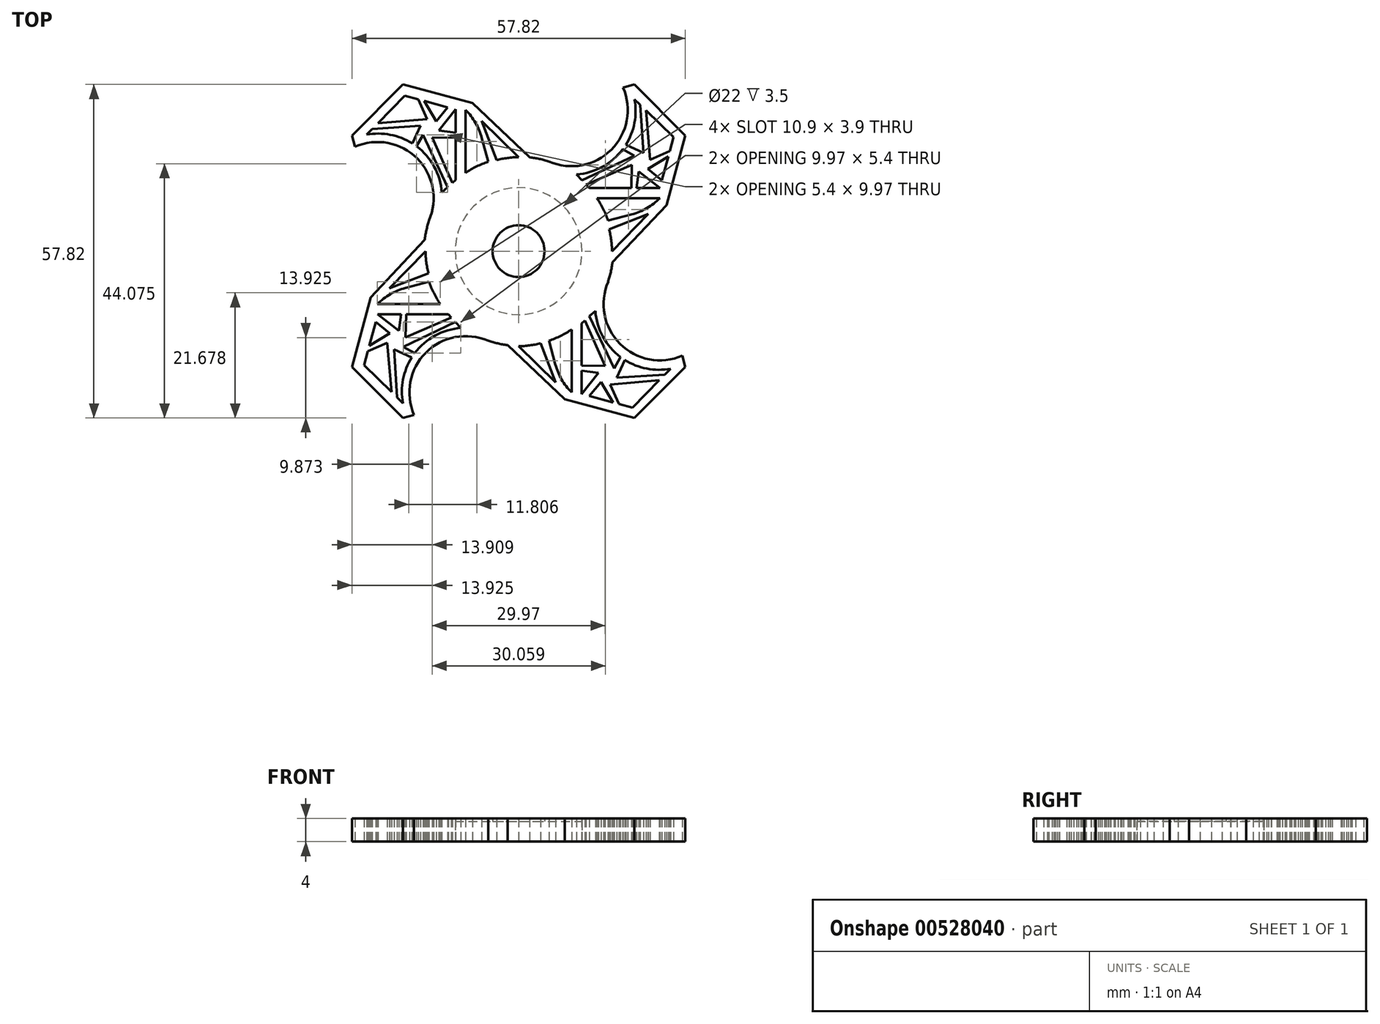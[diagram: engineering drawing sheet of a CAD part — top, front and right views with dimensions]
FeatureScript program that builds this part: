
annotation { "Feature Type Name" : "Feature", "Feature Type Description" : "" }
export const myFeature = defineFeature(function(context is Context, id is Id, definition is map)
    precondition{}
    {
        {
            var Q0;
            Q0=qCreatedBy(makeId("Top.planeOp"),FACE);
            var sketch = newSketch(context, id + "F0", { "sketchPlane" : qUnion([Q0])});
            skCircle(sketch, "E0", {"center": v(0, 0) * mm, "radius": 16.4 * mm});
            skSolve(sketch);
        }
        {
            var Q0;
            Q0 = qSketchRegion(id + "F0", true);
            extrude(context, id + "F1", {"entities" : qUnion([Q0]), "depth" : 4 * mm, "offsetDistance" : 25 * mm});
        }
        {
            var Q0;
            Q0=qCreatedBy(makeId("Top.planeOp"),FACE);
            var sketch = newSketch(context, id + "F2", { "sketchPlane" : qUnion([Q0])});
            skPoint(sketch, "E1", {"position": v(0, 0) * mm});
            skSolve(sketch);
        }
        {
            var Q0;
            Q0=qCreatedBy(makeId("Top.planeOp"),FACE);
            var sketch = newSketch(context, id + "F3", { "sketchPlane" : qUnion([Q0])});
            skLineSegment(sketch, "E2.bottom", {"start": v(-9.18, 9.18) * mm, "end": v(-24.49, 9.18) * mm});
            skLineSegment(sketch, "E2.top", {"start": v(-9.18, 24.49) * mm, "end": v(-24.49, 24.49) * mm});
            skLineSegment(sketch, "E2.left", {"start": v(-9.18, 9.18) * mm, "end": v(-9.18, 24.49) * mm});
            skLineSegment(sketch, "E2.right", {"start": v(-24.49, 9.18) * mm, "end": v(-24.49, 24.49) * mm});
            skPoint(sketch, "E3.oppositeSnap0", {"position": v(-16.84, 9.18) * mm});
            skLineSegment(sketch, "E4.bottom", {"start": v(-9.18, -9.18) * mm, "end": v(-24.49, -9.18) * mm});
            skLineSegment(sketch, "E4.top", {"start": v(-9.18, -24.49) * mm, "end": v(-24.49, -24.49) * mm});
            skLineSegment(sketch, "E4.left", {"start": v(-9.18, -9.18) * mm, "end": v(-9.18, -24.49) * mm});
            skLineSegment(sketch, "E4.right", {"start": v(-24.49, -9.18) * mm, "end": v(-24.49, -24.49) * mm});
            skLineSegment(sketch, "E5.bottom", {"start": v(9.18, -9.18) * mm, "end": v(24.49, -9.18) * mm});
            skLineSegment(sketch, "E5.top", {"start": v(9.18, -24.49) * mm, "end": v(24.49, -24.49) * mm});
            skLineSegment(sketch, "E5.left", {"start": v(9.18, -9.18) * mm, "end": v(9.18, -24.49) * mm});
            skLineSegment(sketch, "E5.right", {"start": v(24.49, -9.18) * mm, "end": v(24.49, -24.49) * mm});
            skLineSegment(sketch, "E6.bottom", {"start": v(9.18, 9.18) * mm, "end": v(24.49, 9.18) * mm});
            skLineSegment(sketch, "E6.top", {"start": v(9.18, 24.49) * mm, "end": v(24.49, 24.49) * mm});
            skLineSegment(sketch, "E6.left", {"start": v(9.18, 9.18) * mm, "end": v(9.18, 24.49) * mm});
            skLineSegment(sketch, "E6.right", {"start": v(24.49, 9.18) * mm, "end": v(24.49, 24.49) * mm});
            skCircle(sketch, "E7", {"center": v(16.84, -16.84) * mm, "radius": 10.82 * mm});
            skCircle(sketch, "E8", {"center": v(16.84, 16.84) * mm, "radius": 10.82 * mm});
            skCircle(sketch, "E9", {"center": v(-16.84, 16.84) * mm, "radius": 10.82 * mm});
            skCircle(sketch, "E10", {"center": v(-16.84, -16.84) * mm, "radius": 10.82 * mm});
            skCircle(sketch, "E11.cCircle", {"center": v(16.84, -16.84) * mm, "radius": 10.82 * mm, "construction": true});
            skLineSegment(sketch, "E11.0", {"start": v(28.9, -20.07) * mm, "end": v(20.07, -28.9) * mm});
            skLineSegment(sketch, "E11.1", {"start": v(20.07, -28.9) * mm, "end": v(8, -25.67) * mm});
            skLineSegment(sketch, "E11.2", {"start": v(8, -25.67) * mm, "end": v(4.76, -13.6) * mm});
            skLineSegment(sketch, "E11.3", {"start": v(4.76, -13.6) * mm, "end": v(13.6, -4.76) * mm});
            skLineSegment(sketch, "E11.4", {"start": v(13.6, -4.76) * mm, "end": v(25.67, -8) * mm});
            skLineSegment(sketch, "E11.5", {"start": v(25.67, -8) * mm, "end": v(28.9, -20.07) * mm});
            skPoint(sketch, "E11.0.midPoint", {"position": v(24.49, -24.49) * mm});
            skCircle(sketch, "E12.cCircle", {"center": v(-16.84, -16.84) * mm, "radius": 10.82 * mm, "construction": true});
            skLineSegment(sketch, "E12.0", {"start": v(-20.07, -28.9) * mm, "end": v(-28.9, -20.07) * mm});
            skLineSegment(sketch, "E12.1", {"start": v(-28.9, -20.07) * mm, "end": v(-25.67, -8) * mm});
            skLineSegment(sketch, "E12.2", {"start": v(-25.67, -8) * mm, "end": v(-13.6, -4.76) * mm});
            skLineSegment(sketch, "E12.3", {"start": v(-13.6, -4.76) * mm, "end": v(-4.76, -13.6) * mm});
            skLineSegment(sketch, "E12.4", {"start": v(-4.76, -13.6) * mm, "end": v(-8, -25.67) * mm});
            skLineSegment(sketch, "E12.5", {"start": v(-8, -25.67) * mm, "end": v(-20.07, -28.9) * mm});
            skPoint(sketch, "E12.0.midPoint", {"position": v(-24.49, -24.49) * mm});
            skCircle(sketch, "E13.cCircle", {"center": v(16.84, 16.84) * mm, "radius": 10.82 * mm, "construction": true});
            skLineSegment(sketch, "E13.0", {"start": v(20.07, 28.9) * mm, "end": v(28.9, 20.07) * mm});
            skLineSegment(sketch, "E13.1", {"start": v(28.9, 20.07) * mm, "end": v(25.67, 8) * mm});
            skLineSegment(sketch, "E13.2", {"start": v(25.67, 8) * mm, "end": v(13.6, 4.76) * mm});
            skLineSegment(sketch, "E13.3", {"start": v(13.6, 4.76) * mm, "end": v(4.76, 13.6) * mm});
            skLineSegment(sketch, "E13.4", {"start": v(4.76, 13.6) * mm, "end": v(8, 25.67) * mm});
            skLineSegment(sketch, "E13.5", {"start": v(8, 25.67) * mm, "end": v(20.07, 28.9) * mm});
            skPoint(sketch, "E13.0.midPoint", {"position": v(24.49, 24.49) * mm});
            skCircle(sketch, "E14.cCircle", {"center": v(-16.84, 16.84) * mm, "radius": 10.82 * mm, "construction": true});
            skLineSegment(sketch, "E14.0", {"start": v(-28.9, 20.07) * mm, "end": v(-20.07, 28.9) * mm});
            skLineSegment(sketch, "E14.1", {"start": v(-20.07, 28.9) * mm, "end": v(-8, 25.67) * mm});
            skLineSegment(sketch, "E14.2", {"start": v(-8, 25.67) * mm, "end": v(-4.76, 13.6) * mm});
            skLineSegment(sketch, "E14.3", {"start": v(-4.76, 13.6) * mm, "end": v(-13.6, 4.76) * mm});
            skLineSegment(sketch, "E14.4", {"start": v(-13.6, 4.76) * mm, "end": v(-25.67, 8) * mm});
            skLineSegment(sketch, "E14.5", {"start": v(-25.67, 8) * mm, "end": v(-28.9, 20.07) * mm});
            skPoint(sketch, "E14.0.midPoint", {"position": v(-24.49, 24.49) * mm});
            skLineSegment(sketch, "E15", {"start": v(-8, 25.67) * mm, "end": v(4.76, 13.6) * mm});
            skLineSegment(sketch, "E16", {"start": v(4.76, 13.6) * mm, "end": v(-4.76, 13.6) * mm});
            skLineSegment(sketch, "E17", {"start": v(25.67, 8) * mm, "end": v(13.6, -4.76) * mm});
            skLineSegment(sketch, "E18", {"start": v(13.6, 4.76) * mm, "end": v(13.6, -4.76) * mm});
            skLineSegment(sketch, "E19", {"start": v(-25.67, -8) * mm, "end": v(-13.6, 4.76) * mm});
            skLineSegment(sketch, "E20", {"start": v(-13.6, 4.76) * mm, "end": v(-13.6, -4.76) * mm});
            skLineSegment(sketch, "E21", {"start": v(8, -25.67) * mm, "end": v(-4.76, -13.6) * mm});
            skLineSegment(sketch, "E22", {"start": v(-4.76, -13.6) * mm, "end": v(4.76, -13.6) * mm});
            skSolve(sketch);
        }
        {
            var Q0;
            Q0 = qSketchRegion(id + "F3", true);
            extrude(context, id + "F4", {"entities" : qUnion([Q0]), "operationType" : NewBodyOperationType.ADD, "depth" : 4 * mm, "offsetDistance" : 25 * mm});
        }
        {
            var Q0;
            Q0=sQuery(id+"F3.wireOp",VERTEX,"E2.right.start");
            var Q1;
            Q1=sQuery(id+"F3.wireOp",VERTEX,"E6.left.end");
            var Q2;
            Q2=sQuery(id+"F3.wireOp",VERTEX,"E5.right.start");
            var Q3;
            Q3=sQuery(id+"F3.wireOp",VERTEX,"E4.top.start");
            var Q4;
            Q4=makeQuery(id+"F1.opExtrude","SWEPT_BODY",BODY,{"disambiguationData":[OSD([sQuery(id+"F0.wireOp",EDGE,"E0")])]});
            hole(context, id + "F5", {"style" : HoleStyle.SIMPLE, "endStyle" : HoleEndStyle.THROUGH, "oppositeDirection" : true, "holeDiameter" : 19.5 * mm, "isTappedThrough" : true, "tappedDepth" : 12 * mm, "tapClearance" : 3, "locations" : qUnion([Q0, Q1, Q2, Q3]), "scope" : qUnion([Q4])});
        }
        {
            var Q0;
            Q0=sQuery(id+"F2.wireOp",VERTEX,"E1");
            var Q1;
            Q1=makeQuery(id+"F1.opExtrude","SWEPT_BODY",BODY,{"disambiguationData":[OSD([sQuery(id+"F0.wireOp",EDGE,"E0")])]});
            hole(context, id + "F6", {"style" : HoleStyle.C_BORE, "endStyle" : HoleEndStyle.THROUGH, "oppositeDirection" : true, "holeDiameter" : 9 * mm, "cBoreDiameter" : 22 * mm, "cBoreDepth" : 3.5 * mm, "isTappedThrough" : true, "tappedDepth" : 12 * mm, "tapClearance" : 3, "locations" : qUnion([Q0]), "scope" : qUnion([Q1])});
        }
        {
            var Q0;
            Q0=qCreatedBy(makeId("Top.planeOp"),FACE);
            var sketch = newSketch(context, id + "F7", { "sketchPlane" : qUnion([Q0])});
            skLineSegment(sketch, "E23", {"start": v(10.93, -12.53) * mm, "end": v(10.93, -24.78) * mm});
            skLineSegment(sketch, "E24", {"start": v(19.76, -27.15) * mm, "end": v(26.35, -20.39) * mm});
            skArc(sketch, "E25", {"start": v(13.31, -10.36) * mm, "mid": v(17.59, -18.28) * mm, "end": v(26.35, -20.39) * mm});
            skLineSegment(sketch, "E26", {"start": v(13.31, -10.36) * mm, "end": v(10.93, -12.53) * mm});
            skLineSegment(sketch, "E27", {"start": v(12.29, -25.13) * mm, "end": v(19.76, -27.15) * mm});
            skLineSegment(sketch, "E28", {"start": v(10.93, -20.73) * mm, "end": v(13.82, -21.12) * mm});
            skLineSegment(sketch, "E29", {"start": v(17.03, -21.92) * mm, "end": v(25.37, -21.4) * mm});
            skLineSegment(sketch, "E30", {"start": v(18.44, -18.88) * mm, "end": v(17.03, -21.92) * mm});
            skLineSegment(sketch, "E31", {"start": v(10.93, -24.78) * mm, "end": v(13.82, -21.12) * mm});
            skLineSegment(sketch, "E32", {"start": v(16.57, -20.33) * mm, "end": v(12.29, -11.3) * mm});
            skLineSegment(sketch, "E33", {"start": v(14.27, -22.7) * mm, "end": v(16.4, -26.24) * mm});
            skLineSegment(sketch, "E34", {"start": v(15.88, -23.1) * mm, "end": v(17.38, -26.5) * mm});
            skLineSegment(sketch, "E35", {"start": v(12.29, -25.13) * mm, "end": v(14.27, -22.7) * mm});
            skLineSegment(sketch, "E36", {"start": v(16.57, -20.33) * mm, "end": v(17.68, -18.36) * mm});
            skLineSegment(sketch, "E37", {"start": v(15.88, -23.1) * mm, "end": v(24.4, -22.39) * mm});
            skLineSegment(sketch, "E38", {"start": v(10.93, -19.83) * mm, "end": v(14.97, -19.93) * mm});
            skLineSegment(sketch, "E39", {"start": v(14.97, -19.93) * mm, "end": v(11.51, -12) * mm});
            skLineSegment(sketch, "E40", {"start": v(6.43, -22.75) * mm, "end": v(0, -16.49) * mm});
            skLineSegment(sketch, "E41", {"start": v(6.43, -22.75) * mm, "end": v(3.8, -15.98) * mm});
            skArc(sketch, "E42", {"start": v(0, -16.49) * mm, "mid": v(1.92, -16.34) * mm, "end": v(3.8, -15.98) * mm});
            skLineSegment(sketch, "E43", {"start": v(12.25, 10.93) * mm, "end": v(24.5, 10.93) * mm});
            skLineSegment(sketch, "E44", {"start": v(26.87, 19.76) * mm, "end": v(20.1, 26.35) * mm});
            skArc(sketch, "E45", {"start": v(10.07, 13.31) * mm, "mid": v(18, 17.59) * mm, "end": v(20.1, 26.35) * mm});
            skLineSegment(sketch, "E46", {"start": v(10.07, 13.31) * mm, "end": v(12.25, 10.93) * mm});
            skLineSegment(sketch, "E47", {"start": v(24.85, 12.29) * mm, "end": v(26.87, 19.76) * mm});
            skLineSegment(sketch, "E48", {"start": v(20.44, 10.93) * mm, "end": v(20.83, 13.82) * mm});
            skLineSegment(sketch, "E49", {"start": v(21.63, 17.03) * mm, "end": v(21.1, 25.37) * mm});
            skLineSegment(sketch, "E50", {"start": v(18.59, 18.44) * mm, "end": v(21.63, 17.03) * mm});
            skLineSegment(sketch, "E51", {"start": v(24.5, 10.93) * mm, "end": v(20.83, 13.82) * mm});
            skLineSegment(sketch, "E52", {"start": v(20.04, 16.57) * mm, "end": v(11, 12.29) * mm});
            skLineSegment(sketch, "E53", {"start": v(22.42, 14.27) * mm, "end": v(25.96, 16.4) * mm});
            skLineSegment(sketch, "E54", {"start": v(22.82, 15.88) * mm, "end": v(26.22, 17.38) * mm});
            skLineSegment(sketch, "E55", {"start": v(24.85, 12.29) * mm, "end": v(22.42, 14.27) * mm});
            skLineSegment(sketch, "E56", {"start": v(20.04, 16.57) * mm, "end": v(18.07, 17.68) * mm});
            skLineSegment(sketch, "E57", {"start": v(22.82, 15.88) * mm, "end": v(22.1, 24.4) * mm});
            skLineSegment(sketch, "E58", {"start": v(19.54, 10.93) * mm, "end": v(19.64, 14.97) * mm});
            skLineSegment(sketch, "E59", {"start": v(19.64, 14.97) * mm, "end": v(11.72, 11.51) * mm});
            skLineSegment(sketch, "E60", {"start": v(22.46, 6.43) * mm, "end": v(16.2, 0) * mm});
            skLineSegment(sketch, "E61", {"start": v(22.46, 6.43) * mm, "end": v(15.7, 3.8) * mm});
            skArc(sketch, "E62", {"start": v(16.2, 0) * mm, "mid": v(16.06, 1.92) * mm, "end": v(15.7, 3.8) * mm});
            skLineSegment(sketch, "E63", {"start": v(-10.93, 12.35) * mm, "end": v(-10.93, 24.6) * mm});
            skLineSegment(sketch, "E64", {"start": v(-19.76, 26.98) * mm, "end": v(-26.35, 20.2) * mm});
            skArc(sketch, "E65", {"start": v(-13.31, 10.18) * mm, "mid": v(-17.59, 18.1) * mm, "end": v(-26.35, 20.2) * mm});
            skLineSegment(sketch, "E66", {"start": v(-13.31, 10.18) * mm, "end": v(-10.93, 12.35) * mm});
            skLineSegment(sketch, "E67", {"start": v(-12.29, 24.95) * mm, "end": v(-19.76, 26.98) * mm});
            skLineSegment(sketch, "E68", {"start": v(-10.93, 20.55) * mm, "end": v(-13.82, 20.94) * mm});
            skLineSegment(sketch, "E69", {"start": v(-17.03, 21.74) * mm, "end": v(-25.37, 21.22) * mm});
            skLineSegment(sketch, "E70", {"start": v(-18.44, 18.7) * mm, "end": v(-17.03, 21.74) * mm});
            skLineSegment(sketch, "E71", {"start": v(-10.93, 24.6) * mm, "end": v(-13.82, 20.94) * mm});
            skLineSegment(sketch, "E72", {"start": v(-16.57, 20.15) * mm, "end": v(-12.29, 11.11) * mm});
            skLineSegment(sketch, "E73", {"start": v(-14.27, 22.53) * mm, "end": v(-16.4, 26.06) * mm});
            skLineSegment(sketch, "E74", {"start": v(-15.88, 22.93) * mm, "end": v(-17.38, 26.33) * mm});
            skLineSegment(sketch, "E75", {"start": v(-12.29, 24.95) * mm, "end": v(-14.27, 22.53) * mm});
            skLineSegment(sketch, "E76", {"start": v(-16.57, 20.15) * mm, "end": v(-17.68, 18.18) * mm});
            skLineSegment(sketch, "E77", {"start": v(-15.88, 22.93) * mm, "end": v(-24.4, 22.2) * mm});
            skLineSegment(sketch, "E78", {"start": v(-10.93, 19.65) * mm, "end": v(-14.97, 19.75) * mm});
            skLineSegment(sketch, "E79", {"start": v(-14.97, 19.75) * mm, "end": v(-11.51, 11.82) * mm});
            skLineSegment(sketch, "E80", {"start": v(-6.43, 22.57) * mm, "end": v(0, 16.3) * mm});
            skLineSegment(sketch, "E81", {"start": v(-6.43, 22.57) * mm, "end": v(-3.8, 15.8) * mm});
            skArc(sketch, "E82", {"start": v(0, 16.3) * mm, "mid": v(-1.92, 16.16) * mm, "end": v(-3.8, 15.8) * mm});
            skLineSegment(sketch, "E83", {"start": v(-12.2, -10.93) * mm, "end": v(-24.43, -10.93) * mm});
            skLineSegment(sketch, "E84", {"start": v(-26.81, -19.76) * mm, "end": v(-20.04, -26.35) * mm});
            skArc(sketch, "E85", {"start": v(-10.02, -13.31) * mm, "mid": v(-17.94, -17.59) * mm, "end": v(-20.04, -26.35) * mm});
            skLineSegment(sketch, "E86", {"start": v(-10.02, -13.31) * mm, "end": v(-12.2, -10.93) * mm});
            skLineSegment(sketch, "E87", {"start": v(-24.8, -12.29) * mm, "end": v(-26.81, -19.76) * mm});
            skLineSegment(sketch, "E88", {"start": v(-20.38, -10.93) * mm, "end": v(-20.77, -13.82) * mm});
            skLineSegment(sketch, "E89", {"start": v(-21.58, -17.03) * mm, "end": v(-21.05, -25.37) * mm});
            skLineSegment(sketch, "E90", {"start": v(-18.53, -18.44) * mm, "end": v(-21.58, -17.03) * mm});
            skLineSegment(sketch, "E91", {"start": v(-24.43, -10.93) * mm, "end": v(-20.77, -13.82) * mm});
            skLineSegment(sketch, "E92", {"start": v(-19.99, -16.57) * mm, "end": v(-10.95, -12.29) * mm});
            skLineSegment(sketch, "E93", {"start": v(-22.37, -14.27) * mm, "end": v(-25.9, -16.4) * mm});
            skLineSegment(sketch, "E94", {"start": v(-22.77, -15.88) * mm, "end": v(-26.17, -17.38) * mm});
            skLineSegment(sketch, "E95", {"start": v(-24.8, -12.29) * mm, "end": v(-22.37, -14.27) * mm});
            skLineSegment(sketch, "E96", {"start": v(-19.99, -16.57) * mm, "end": v(-18.01, -17.68) * mm});
            skLineSegment(sketch, "E97", {"start": v(-22.77, -15.88) * mm, "end": v(-22.04, -24.4) * mm});
            skLineSegment(sketch, "E98", {"start": v(-19.49, -10.93) * mm, "end": v(-19.59, -14.97) * mm});
            skLineSegment(sketch, "E99", {"start": v(-19.59, -14.97) * mm, "end": v(-11.66, -11.51) * mm});
            skLineSegment(sketch, "E100", {"start": v(-22.4, -6.43) * mm, "end": v(-16.14, 0) * mm});
            skLineSegment(sketch, "E101", {"start": v(-22.4, -6.43) * mm, "end": v(-15.64, -3.8) * mm});
            skArc(sketch, "E102", {"start": v(-16.14, 0) * mm, "mid": v(-16, -1.92) * mm, "end": v(-15.64, -3.8) * mm});
            skSolve(sketch);
        }
        {
            var Q0;
            Q0 = qSketchRegion(id + "F7", true);
            extrude(context, id + "F8", {"entities" : qUnion([Q0]), "operationType" : NewBodyOperationType.REMOVE, "endBound" : BoundingType.THROUGH_ALL, "depth" : 25 * mm, "offsetDistance" : 25 * mm});
        }
        {
            var Q0;
            Q0=makeQuery(id+"F1.opExtrude","SWEPT_BODY",BODY,{"disambiguationData":[OSD([sQuery(id+"F0.wireOp",EDGE,"E0")])]});
            var Q1;
            Q1=makeQuery(id+"F6.hole-0.boolean.opBoolean","COPY",EDGE,{"derivedFrom":makeQuery(id+"F6.hole-0.opRevolve","SWEPT_EDGE",EDGE,{"disambiguationData":[OSD([sQuery(id+"F6.hole-0.sketch.wireOp",EDGE,"cbore_start_line_1"),sQuery(id+"F6.hole-0.sketch.wireOp",EDGE,"core_line_2")])]})});
            transform(context, id + "F9", {"entities" : qUnion([Q0]), "transformType" : TransformType.TRANSLATION_3D, "dx" : 0 * mm, "dy" : 0 * mm, "dz" : 4 * mm, "makeCopy" : true});
        }
        {
            var Q0;
            Q0=makeQuery(id+"F9.opPattern","COPY",BODY,{"derivedFrom":makeQuery(id+"F1.opExtrude","SWEPT_BODY",BODY,{"disambiguationData":[OSD([sQuery(id+"F0.wireOp",EDGE,"E0")])]}),"instanceName":"1"});
            deleteBodies(context, id + "F10", {"entities" : qUnion([Q0])});
        }
    });
